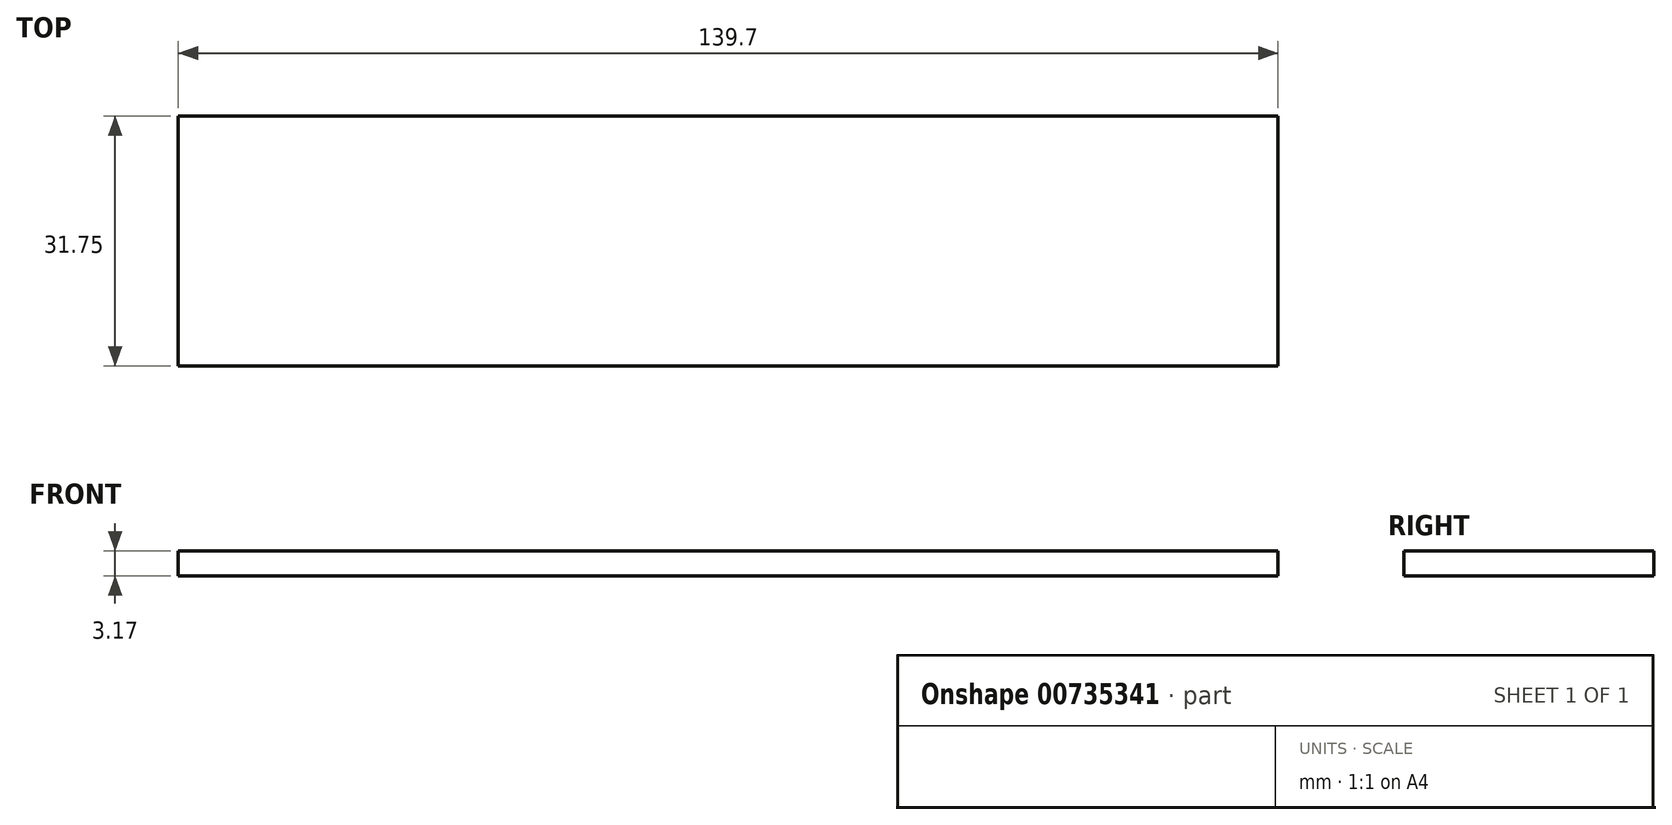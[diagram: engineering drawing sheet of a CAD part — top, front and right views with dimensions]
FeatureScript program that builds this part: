
annotation { "Feature Type Name" : "Feature", "Feature Type Description" : "" }
export const myFeature = defineFeature(function(context is Context, id is Id, definition is map)
    precondition{}
    {
        {
            var Q0;
            Q0=qCreatedBy(makeId("Top.planeOp"),FACE);
            var sketch = newSketch(context, id + "F0", { "sketchPlane" : qUnion([Q0])});
            skLineSegment(sketch, "E0.bottom", {"start": v(-39.96, 0) * mm, "end": v(99.74, 0) * mm});
            skLineSegment(sketch, "E0.top", {"start": v(-39.96, 31.75) * mm, "end": v(99.74, 31.75) * mm});
            skLineSegment(sketch, "E0.left", {"start": v(-39.96, 0) * mm, "end": v(-39.96, 31.75) * mm});
            skLineSegment(sketch, "E0.right", {"start": v(99.74, 0) * mm, "end": v(99.74, 31.75) * mm});
            skSolve(sketch);
        }
        {
            var Q0;
            Q0 = qSketchRegion(id + "F0", true);
            extrude(context, id + "F1", {"entities" : qUnion([Q0]), "depth" : 3.17 * mm, "offsetDistance" : 25.4 * mm});
        }
    });
